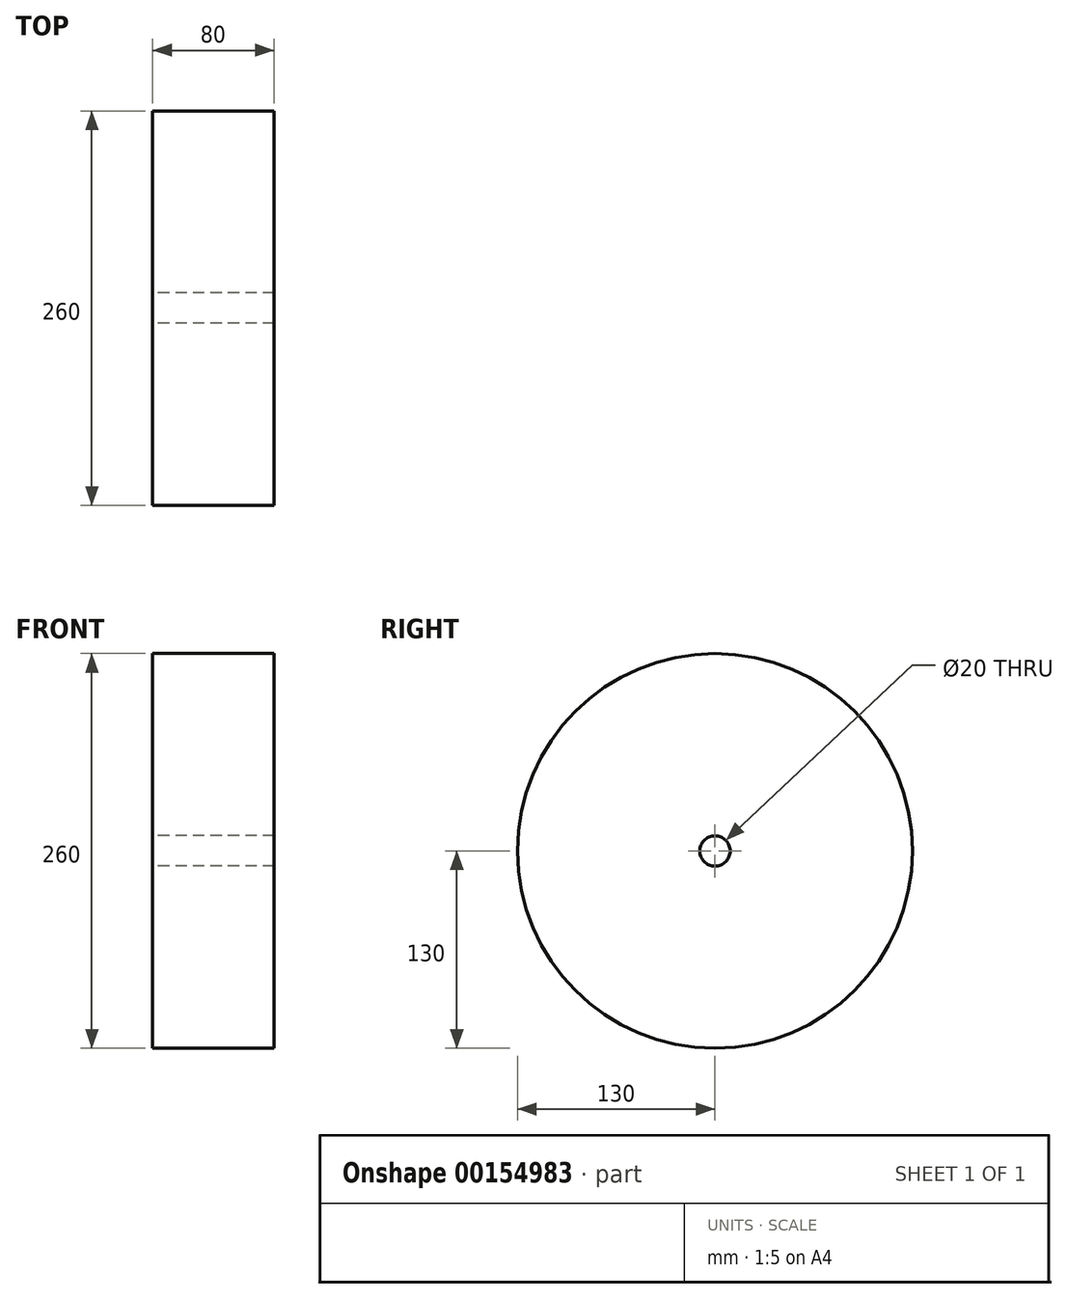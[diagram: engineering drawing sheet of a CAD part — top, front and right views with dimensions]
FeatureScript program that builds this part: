
annotation { "Feature Type Name" : "Feature", "Feature Type Description" : "" }
export const myFeature = defineFeature(function(context is Context, id is Id, definition is map)
    precondition{}
    {
        {
            var Q0;
            Q0=qCreatedBy(makeId("Right.planeOp"),FACE);
            var sketch = newSketch(context, id + "F0", { "sketchPlane" : qUnion([Q0])});
            skCircle(sketch, "E0", {"center": v(0, 0) * mm, "radius": 130 * mm});
            skSolve(sketch);
        }
        {
            var Q0;
            Q0=makeQuery(id+"F0.imprint","IMPRINT",FACE,{"disambiguationData":[TD([[makeQuery(id+"F0.imprint","IMPRINT",EDGE,{"derivedFrom":sQuery(id+"F0.wireOp",EDGE,"E0")}),1.0]])]});
            extrude(context, id + "F1", {"entities" : qUnion([Q0]), "depth" : 80 * mm});
        }
        {
            var Q0;
            Q0=makeQuery(id+"F1.opExtrude","CAP_FACE",FACE,{"disambiguationData":[OSD([sQuery(id+"F0.wireOp",EDGE,"E0")])],"isStart":true});
            var sketch = newSketch(context, id + "F2", { "sketchPlane" : qUnion([Q0])});
            skCircle(sketch, "E1", {"center": v(0, 0) * mm, "radius": 10 * mm});
            skSolve(sketch);
        }
        {
            var Q0;
            Q0=makeQuery(id+"F2.imprint","IMPRINT",FACE,{"disambiguationData":[TD([[makeQuery(id+"F2.imprint","IMPRINT",EDGE,{"derivedFrom":sQuery(id+"F2.wireOp",EDGE,"E1")}),1.0]])]});
            extrude(context, id + "F3", {"entities" : qUnion([Q0]), "operationType" : NewBodyOperationType.REMOVE, "endBound" : BoundingType.UP_TO_NEXT, "oppositeDirection" : true, "depth" : 25 * mm});
        }
    });
